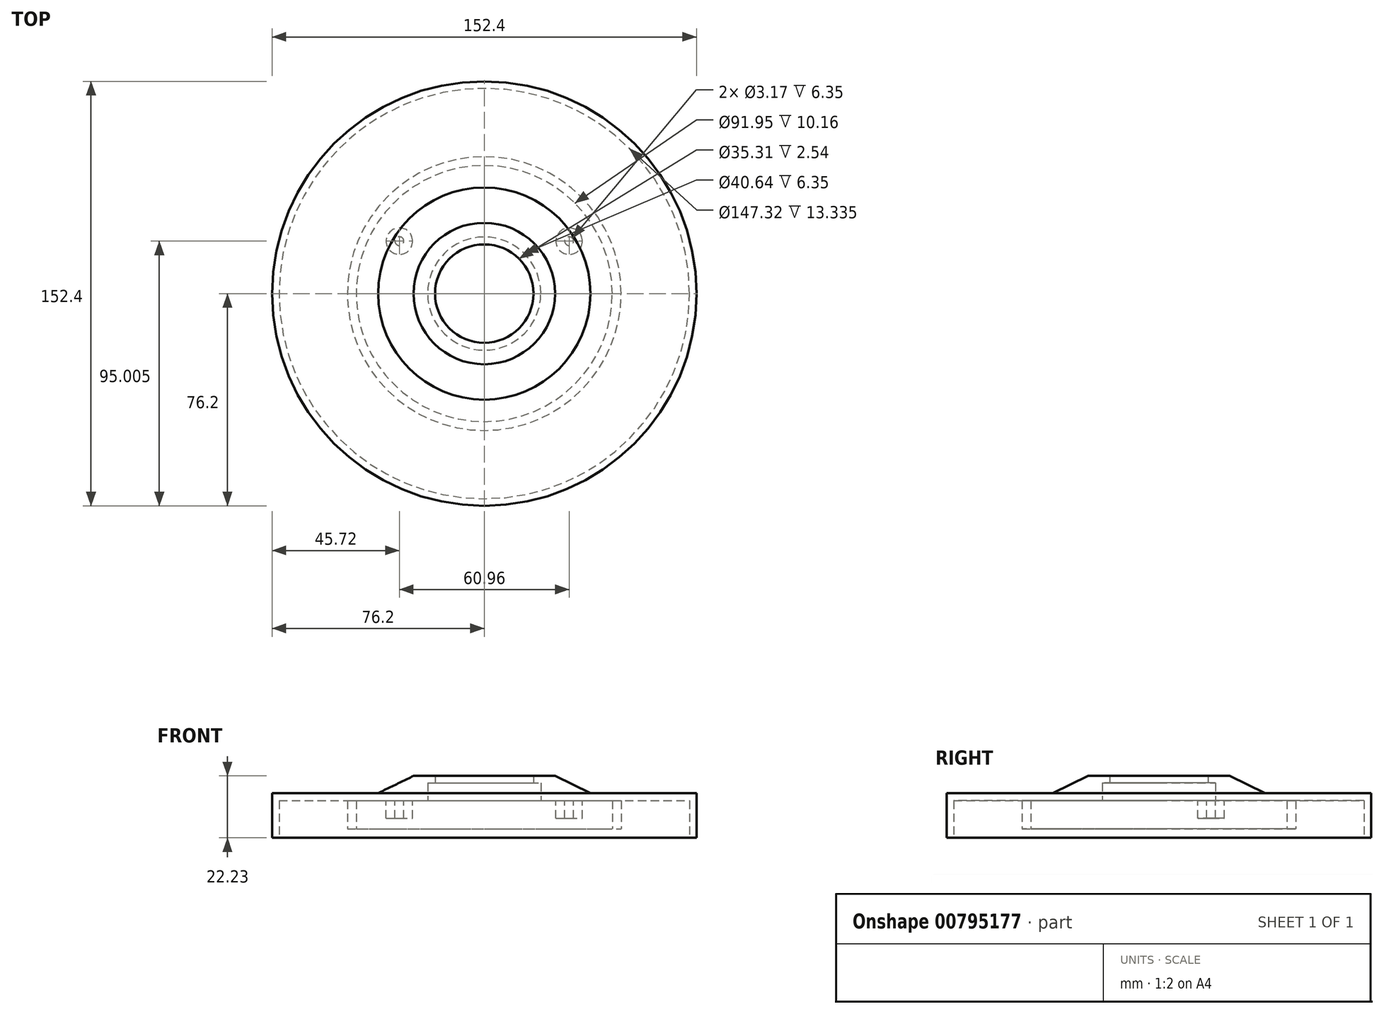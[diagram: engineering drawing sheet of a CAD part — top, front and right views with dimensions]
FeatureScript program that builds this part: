
annotation { "Feature Type Name" : "Feature", "Feature Type Description" : "" }
export const myFeature = defineFeature(function(context is Context, id is Id, definition is map)
    precondition{}
    {
        {
            var Q0;
            Q0=qCreatedBy(makeId("Top.planeOp"),FACE);
            var sketch = newSketch(context, id + "F0", { "sketchPlane" : qUnion([Q0])});
            skCircle(sketch, "E0", {"center": v(0, 0) * mm, "radius": 76.2 * mm});
            skSolve(sketch);
        }
        {
            var Q0;
            Q0 = qSketchRegion(id + "F0", true);
            extrude(context, id + "F1", {"entities" : qUnion([Q0]), "depth" : 19.05 * mm, "offsetDistance" : 25.4 * mm});
        }
        {
            var Q0;
            Q0=makeQuery(id+"F1.opExtrude","CAP_FACE",FACE,{"disambiguationData":[OSD([sQuery(id+"F0.wireOp",EDGE,"E0")])],"isStart":true});
            var sketch = newSketch(context, id + "F2", { "sketchPlane" : qUnion([Q0])});
            skCircle(sketch, "E1", {"center": v(0, 0) * mm, "radius": 45.97 * mm});
            skSolve(sketch);
        }
        {
            var Q0;
            Q0 = qSketchRegion(id + "F2", true);
            extrude(context, id + "F3", {"entities" : qUnion([Q0]), "operationType" : NewBodyOperationType.REMOVE, "oppositeDirection" : true, "depth" : 10.16 * mm, "offsetDistance" : 25.4 * mm});
        }
        {
            var Q0;
            Q0=qCreatedBy(makeId("Front.planeOp"),FACE);
            var sketch = newSketch(context, id + "F4", { "sketchPlane" : qUnion([Q0])});
            skLineSegment(sketch, "E2", {"start": v(-17.65, 16.51) * mm, "end": v(-17.65, 19.05) * mm});
            skLineSegment(sketch, "E3", {"start": v(-17.65, 19.05) * mm, "end": v(0, 19.05) * mm});
            skLineSegment(sketch, "E4", {"start": v(0, 19.05) * mm, "end": v(0, 10.16) * mm});
            skLineSegment(sketch, "E5", {"start": v(0, 10.16) * mm, "end": v(-20.32, 10.16) * mm});
            skLineSegment(sketch, "E6", {"start": v(-20.32, 10.16) * mm, "end": v(-20.32, 16.51) * mm});
            skLineSegment(sketch, "E7", {"start": v(-20.32, 16.51) * mm, "end": v(-17.65, 16.51) * mm});
            skSolve(sketch);
        }
        {
            var Q0;
            Q0 = qSketchRegion(id + "F4", true);
            var Q1;
            Q1=sQuery(id+"F4.wireOp",EDGE,"E4");
            revolve(context, id + "F5", {"operationType" : NewBodyOperationType.REMOVE, "surfaceOperationType" : NewSurfaceOperationType.NEW, "entities" : qUnion([Q0]), "axis" : qUnion([Q1]), "revolveType" : RevolveType.FULL, "oppositeDirection" : true});
        }
        {
            var Q0;
            Q0=qCreatedBy(makeId("Right.planeOp"),FACE);
            var sketch = newSketch(context, id + "F6", { "sketchPlane" : qUnion([Q0])});
            skLineSegment(sketch, "E8", {"start": v(-25.4, 19.05) * mm, "end": v(-38.1, 12.88) * mm});
            skLineSegment(sketch, "E9", {"start": v(-38.1, 12.88) * mm, "end": v(-86.35, 12.88) * mm});
            skLineSegment(sketch, "E10", {"start": v(-86.35, 12.88) * mm, "end": v(-86.35, 29.32) * mm});
            skLineSegment(sketch, "E11", {"start": v(-86.35, 29.32) * mm, "end": v(0, 29.32) * mm});
            skLineSegment(sketch, "E12", {"start": v(0, 29.32) * mm, "end": v(0, 19.05) * mm});
            skLineSegment(sketch, "E13", {"start": v(0, 19.05) * mm, "end": v(-25.4, 19.05) * mm});
            skSolve(sketch);
        }
        {
            var Q0;
            Q0 = qSketchRegion(id + "F6", true);
            var Q1;
            Q1=sQuery(id+"F6.wireOp",EDGE,"E12");
            revolve(context, id + "F7", {"operationType" : NewBodyOperationType.REMOVE, "surfaceOperationType" : NewSurfaceOperationType.NEW, "entities" : qUnion([Q0]), "axis" : qUnion([Q1]), "revolveType" : RevolveType.FULL, "oppositeDirection" : true});
        }
        {
            var Q0;
            Q0=makeQuery(id+"F1.opExtrude","CAP_FACE",FACE,{"disambiguationData":[OSD([sQuery(id+"F0.wireOp",EDGE,"E0")])],"isStart":true});
            var sketch = newSketch(context, id + "F8", { "sketchPlane" : qUnion([Q0])});
            skCircle(sketch, "E14", {"center": v(0, 0) * mm, "radius": 49.15 * mm});
            skCircle(sketch, "E15", {"center": v(0, 0) * mm, "radius": 73.66 * mm});
            skSolve(sketch);
        }
        {
            var Q0;
            Q0 = qSketchRegion(id + "F8", true);
            var Q1;
            Q1=makeQuery(id+"F3.boolean.opBoolean","COPY",FACE,{"derivedFrom":makeQuery(id+"F3.opExtrude","CAP_FACE",FACE,{"disambiguationData":[OSD([sQuery(id+"F2.wireOp",EDGE,"E1")])],"isStart":false})});
            extrude(context, id + "F9", {"entities" : qUnion([Q0]), "operationType" : NewBodyOperationType.REMOVE, "endBound" : BoundingType.UP_TO_SURFACE, "oppositeDirection" : true, "depth" : 25.4 * mm, "endBoundEntityFace" : qUnion([Q1]), "offsetDistance" : 25.4 * mm});
        }
        {
            var Q0;
            {var subQ0=sQuery(id+"F0.wireOp",EDGE,"E0");Q0=makeQuery(id+"F9.boolean.opBoolean","SPLIT",FACE,{"disambiguationData":[TD([makeQuery(id+"F1.opExtrude","SWEPT_FACE",FACE,{"disambiguationData":[OSD([subQ0])]})])],"derivedFrom":makeQuery(id+"F1.opExtrude","CAP_FACE",FACE,{"disambiguationData":[OSD([subQ0])],"isStart":true})});}
            var sketch = newSketch(context, id + "F10", { "sketchPlane" : qUnion([Q0])});
            skCircle(sketch, "E16.0.0", {"center": v(0, 0) * mm, "radius": 76.2 * mm});
            skCircle(sketch, "E17.0", {"center": v(0, 0) * mm, "radius": 73.66 * mm});
            skSolve(sketch);
        }
        {
            var Q0;
            Q0 = qSketchRegion(id + "F10", true);
            extrude(context, id + "F11", {"entities" : qUnion([Q0]), "operationType" : NewBodyOperationType.ADD, "depth" : 3.17 * mm, "offsetDistance" : 25.4 * mm});
        }
        {
            var Q0;
            Q0=qCreatedBy(makeId("Front.planeOp"),FACE);
            var sketch = newSketch(context, id + "F12", { "sketchPlane" : qUnion([Q0])});
            skLineSegment(sketch, "E18.bottom", {"start": v(208.33, 87.85) * mm, "end": v(-274.72, 87.85) * mm});
            skLineSegment(sketch, "E18.top", {"start": v(208.33, -110.15) * mm, "end": v(-274.72, -110.15) * mm});
            skLineSegment(sketch, "E18.left", {"start": v(208.33, 87.85) * mm, "end": v(208.33, -110.15) * mm});
            skLineSegment(sketch, "E18.right", {"start": v(-274.72, 87.85) * mm, "end": v(-274.72, -110.15) * mm});
            skSolve(sketch);
        }
        {
            var Q0;
            Q0=makeQuery(id+"F3.boolean.opBoolean","COPY",FACE,{"derivedFrom":makeQuery(id+"F3.opExtrude","CAP_FACE",FACE,{"disambiguationData":[OSD([sQuery(id+"F2.wireOp",EDGE,"E1")])],"isStart":false})});
            var sketch = newSketch(context, id + "F13", { "sketchPlane" : qUnion([Q0])});
            skPoint(sketch, "E19", {"position": v(30.48, -18.8) * mm});
            skPoint(sketch, "E20", {"position": v(-30.48, -18.8) * mm});
            skSolve(sketch);
        }
        {
            var Q0;
            Q0=makeQuery(id+"F13.imprint","IMPRINT",FACE,{"disambiguationData":[TD([[makeQuery(id+"F13.imprint","IMPRINT",EDGE,{"derivedFrom":makeQuery(id+"F3.boolean.opBoolean","COPY",EDGE,{"derivedFrom":makeQuery(id+"F3.opExtrude","CAP_EDGE",EDGE,{"disambiguationData":[OSD([sQuery(id+"F2.wireOp",EDGE,"E1")])],"isStart":false})})}),1.0]])]});
            var sketch = newSketch(context, id + "F14", { "sketchPlane" : qUnion([Q0])});
            skCircle(sketch, "E21", {"center": v(30.48, -18.8) * mm, "radius": 4.76 * mm});
            skCircle(sketch, "E22", {"center": v(-30.48, -18.8) * mm, "radius": 4.76 * mm});
            skCircle(sketch, "E23", {"center": v(30.48, -18.8) * mm, "radius": 1.59 * mm});
            skCircle(sketch, "E24", {"center": v(-30.48, -18.8) * mm, "radius": 1.59 * mm});
            skSolve(sketch);
        }
        {
            var Q0;
            Q0 = qSketchRegion(id + "F14", true);
            extrude(context, id + "F15", {"entities" : qUnion([Q0]), "operationType" : NewBodyOperationType.ADD, "depth" : 6.35 * mm, "offsetDistance" : 25.4 * mm});
        }
    });
